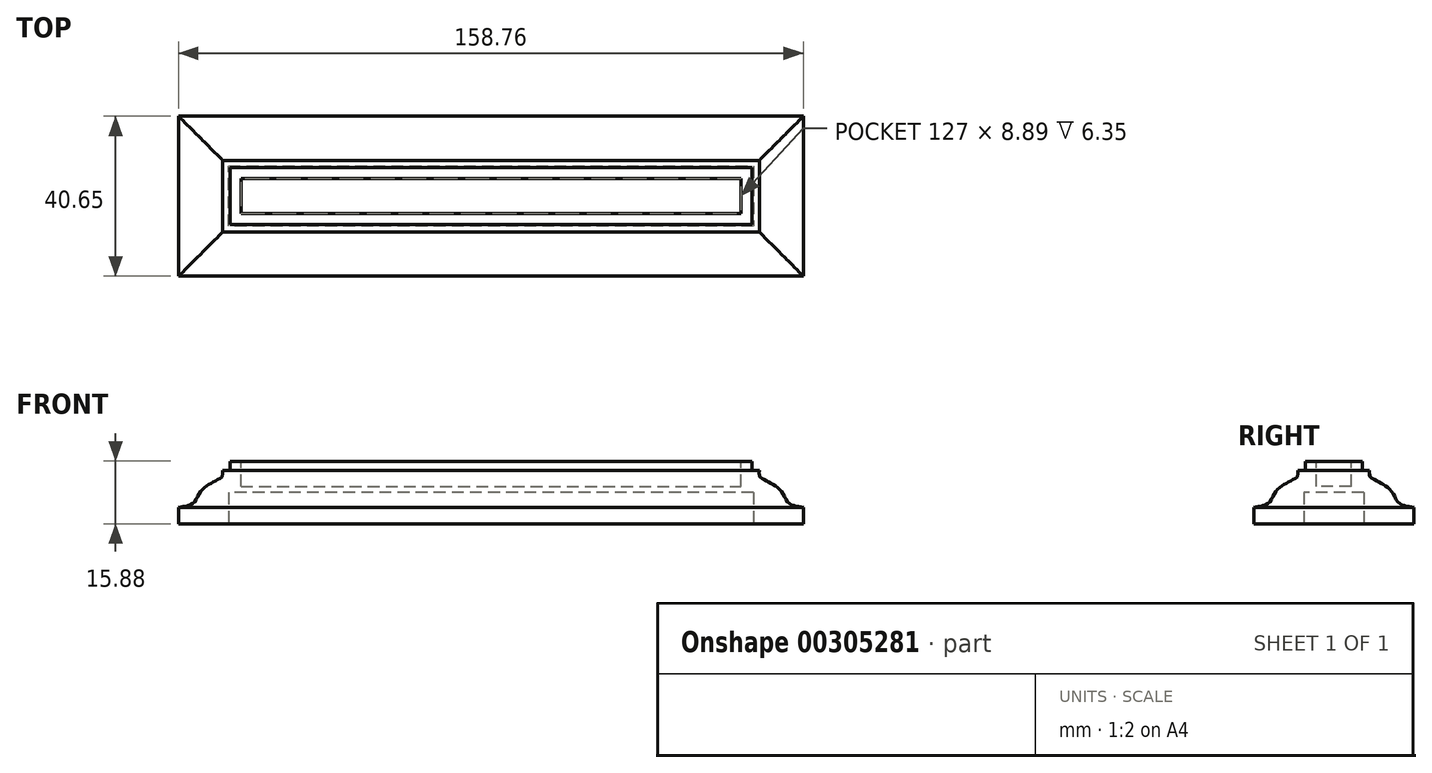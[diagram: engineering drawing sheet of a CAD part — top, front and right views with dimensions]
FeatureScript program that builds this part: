
annotation { "Feature Type Name" : "Feature", "Feature Type Description" : "" }
export const myFeature = defineFeature(function(context is Context, id is Id, definition is map)
    precondition{}
    {
        {
            var Q0;
            Q0=qCreatedBy(makeId("Top.planeOp"),FACE);
            var sketch = newSketch(context, id + "F0", { "sketchPlane" : qUnion([Q0])});
            skLineSegment(sketch, "E0.bottom", {"start": v(-63.5, 0) * mm, "end": v(63.5, 0) * mm});
            skLineSegment(sketch, "E0.top", {"start": v(-63.5, -8.89) * mm, "end": v(63.5, -8.9) * mm});
            skLineSegment(sketch, "E0.left", {"start": v(-63.5, 0) * mm, "end": v(-63.5, -8.89) * mm});
            skLineSegment(sketch, "E0.right", {"start": v(63.5, 0) * mm, "end": v(63.5, -8.89) * mm});
            skSolve(sketch);
        }
        {
            var Q0;
            Q0=qCreatedBy(makeId("Right.planeOp"),FACE);
            var sketch = newSketch(context, id + "F1", { "sketchPlane" : qUnion([Q0])});
            skLineSegment(sketch, "E1", {"start": v(0, 0) * mm, "end": v(15.88, 0) * mm});
            skLineSegment(sketch, "E2", {"start": v(15.88, 0) * mm, "end": v(15.88, 4.18) * mm});
            skLineSegment(sketch, "E3", {"start": v(2.78, 15.88) * mm, "end": v(0, 15.88) * mm});
            skLineSegment(sketch, "E4", {"start": v(0, 15.88) * mm, "end": v(0, 0) * mm});
            skLineSegment(sketch, "E5.bottom", {"start": v(0, 15.88) * mm, "end": v(2.78, 15.88) * mm});
            skLineSegment(sketch, "E5.top", {"start": v(2.78, 13.57) * mm, "end": v(4.66, 13.57) * mm});
            skLineSegment(sketch, "E6.bottom", {"start": v(15.88, 0) * mm, "end": v(0, 0) * mm});
            skLineSegment(sketch, "E6.right", {"start": v(0, 0) * mm, "end": v(0, 4.18) * mm});
            skLineSegment(sketch, "E7", {"start": v(2.78, 15.88) * mm, "end": v(2.78, 13.57) * mm});
            skPoint(sketch, "E8.1.internal.orphan", {"position": v(4.66, 16.7) * mm});
            skFitSpline(sketch, "E9", {"points": [v(15.87, 4.18) * mm, v(12.11, 5.27) * mm, v(9.78, 8.77) * mm, v(4.9, 11.84) * mm, v(4.66, 13.57) * mm], "startDerivative": vector(-15.34, 1.9) * mm, "endDerivative": vector(-0.47, 19.04) * mm});
            skSolve(sketch);
        }
        {
            var Q0;
            Q0=makeQuery(id+"F1.imprint","IMPRINT",FACE,{"disambiguationData":[TD([[makeQuery(id+"F1.imprint","IMPRINT",EDGE,{"derivedFrom":sQuery(id+"F1.wireOp",EDGE,"E4")}),1.0]])]});
            var Q1;
            Q1=sQuery(id+"F0.wireOp",EDGE,"E0.bottom");
            var Q2;
            Q2=sQuery(id+"F0.wireOp",EDGE,"E0.left");
            var Q3;
            Q3=sQuery(id+"F0.wireOp",EDGE,"E0.top");
            var Q4;
            Q4=sQuery(id+"F0.wireOp",EDGE,"E0.right");
            sweep(context, id + "F2", {"profiles" : qUnion([Q0]), "path" : qUnion([Q1, Q2, Q3, Q4])});
        }
        {
            var Q0;
            Q0=qCreatedBy(makeId("Top.planeOp"),FACE);
            var sketch = newSketch(context, id + "F3", { "sketchPlane" : qUnion([Q0])});
            skPoint(sketch, "E10.0", {"position": v(63.5, 0) * mm});
            skPoint(sketch, "E11.0", {"position": v(63.5, -8.89) * mm});
            skPoint(sketch, "E12.0", {"position": v(-63.5, -8.89) * mm});
            skPoint(sketch, "E13.0", {"position": v(-63.5, 0) * mm});
            skLineSegment(sketch, "E14.bottom", {"start": v(-63.5, 0) * mm, "end": v(63.5, 0) * mm});
            skLineSegment(sketch, "E14.top", {"start": v(-63.5, -8.89) * mm, "end": v(63.5, -8.89) * mm});
            skLineSegment(sketch, "E14.left", {"start": v(63.5, 0) * mm, "end": v(63.5, -8.89) * mm});
            skLineSegment(sketch, "E14.right", {"start": v(-63.5, 0) * mm, "end": v(-63.5, -8.89) * mm});
            skSolve(sketch);
        }
        {
            var Q0;
            Q0=qSketchRegion(id+"F3",true);
            extrude(context, id + "F4", {"entities" : qUnion([Q0]), "operationType" : NewBodyOperationType.ADD, "depth" : 9.52 * mm});
        }
        {
            var Q0;
            Q0=makeQuery(id+"F4.boolean.opBoolean","MERGE",FACE,{"derivedFrom":[makeQuery(id+"F2.opSweep","SWEPT_FACE",FACE,{"disambiguationData":[OSD([sQuery(id+"F0.wireOp",EDGE,"E0.bottom"),sQuery(id+"F1.wireOp",EDGE,"E6.bottom")])]}),makeQuery(id+"F4.opExtrude","CAP_FACE",FACE,{"disambiguationData":[OSD([sQuery(id+"F3.wireOp",EDGE,"E14.bottom"),sQuery(id+"F3.wireOp",EDGE,"E14.top"),sQuery(id+"F3.wireOp",EDGE,"E14.left"),sQuery(id+"F3.wireOp",EDGE,"E14.right")])],"isStart":true})]});
            var sketch = newSketch(context, id + "F5", { "sketchPlane" : qUnion([Q0])});
            skLineSegment(sketch, "E15.0", {"start": v(66.67, 12.06) * mm, "end": v(-66.67, 12.06) * mm});
            skLineSegment(sketch, "E15.1", {"start": v(66.67, -3.17) * mm, "end": v(66.67, 12.06) * mm});
            skLineSegment(sketch, "E15.2", {"start": v(-66.67, -3.18) * mm, "end": v(66.67, -3.17) * mm});
            skLineSegment(sketch, "E15.3", {"start": v(-66.67, 12.06) * mm, "end": v(-66.67, -3.18) * mm});
            skSolve(sketch);
        }
        {
            var Q0;
            Q0=qSketchRegion(id+"F5",true);
            extrude(context, id + "F6", {"entities" : qUnion([Q0]), "operationType" : NewBodyOperationType.REMOVE, "oppositeDirection" : true, "depth" : 7.89 * mm});
        }
    });
